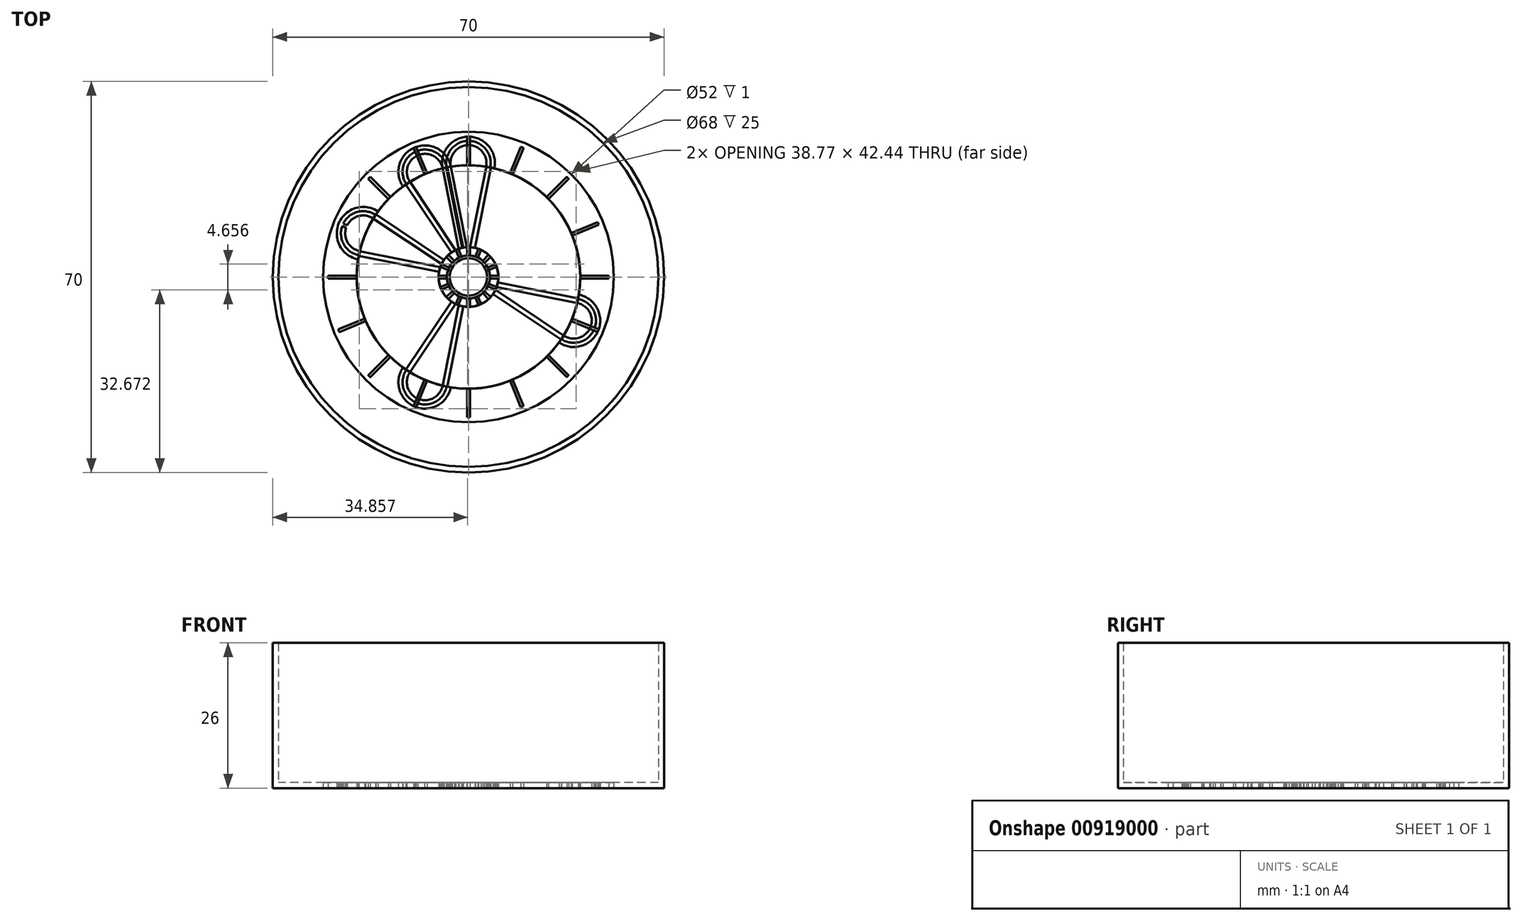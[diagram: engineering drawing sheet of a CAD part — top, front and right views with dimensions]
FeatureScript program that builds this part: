
annotation { "Feature Type Name" : "Feature", "Feature Type Description" : "" }
export const myFeature = defineFeature(function(context is Context, id is Id, definition is map)
    precondition{}
    {
        {
            var Q0;
            Q0=qCreatedBy(makeId("Top.planeOp"),FACE);
            var sketch = newSketch(context, id + "F0", { "sketchPlane" : qUnion([Q0])});
            skCircle(sketch, "E0", {"center": v(0, 0) * mm, "radius": 20 * mm});
            skLineSegment(sketch, "E1", {"start": v(0, 3.84) * mm, "end": v(0, 25.12) * mm});
            skLineSegment(sketch, "E2", {"start": v(-1.04, 5.24) * mm, "end": v(-3.9, 19.62) * mm});
            skLineSegment(sketch, "E3.trimOffspring", {"start": v(-0.3, 5.34) * mm, "end": v(-3.16, 19.75) * mm});
            skCircle(sketch, "E4", {"center": v(0, 0) * mm, "radius": 3.84 * mm});
            skCircle(sketch, "E5.0", {"center": v(0, 0) * mm, "radius": 5.34 * mm});
            skLineSegment(sketch, "E6.trimOffspring", {"start": v(1.04, 5.24) * mm, "end": v(3.9, 19.62) * mm});
            skArc(sketch, "E7", {"start": v(-3.9, 19.62) * mm, "mid": v(0, 24.37) * mm, "end": v(3.9, 19.62) * mm});
            skLineSegment(sketch, "E8.0", {"start": v(0.3, 5.34) * mm, "end": v(3.16, 19.75) * mm});
            skArc(sketch, "E9.0", {"start": v(-4.63, 19.46) * mm, "mid": v(0, 25.12) * mm, "end": v(4.63, 19.46) * mm});
            skArc(sketch, "E10", {"start": v(-3.16, 19.75) * mm, "mid": v(0, 23.6) * mm, "end": v(3.16, 19.75) * mm});
            skLineSegment(sketch, "E11.0", {"start": v(-1.14, 5.22) * mm, "end": v(-4, 19.6) * mm});
            skLineSegment(sketch, "E12.0", {"start": v(1.14, 5.22) * mm, "end": v(4, 19.6) * mm});
            skCircle(sketch, "E13", {"center": v(0, 0) * mm, "radius": 26 * mm});
            skPoint(sketch, "E14.orphan", {"position": v(0, 20) * mm});
            skLineSegment(sketch, "E15.0", {"start": v(0.25, 3.84) * mm, "end": v(0.25, 25.11) * mm});
            skLineSegment(sketch, "E16.0", {"start": v(-0.25, 3.84) * mm, "end": v(-0.25, 25.11) * mm});
            skSolve(sketch);
        }
        {
            var Q0;
            {var subQ0=sQuery(id+"F0.wireOp",EDGE,"E6.trimOffspring");Q0=makeQuery(id+"F0.imprint","IMPRINT",FACE,{"disambiguationData":[TD([[makeQuery(id+"F0.imprint","IMPRINT",EDGE,{"derivedFrom":subQ0}),1.0]])]});}
            var Q1;
            {var subQ0=sQuery(id+"F0.wireOp",EDGE,"E4");var subQ1=sQuery(id+"F0.wireOp",EDGE,"E1");var subQ2=makeQuery(id+"F0.imprint","INTERSECT",VERTEX,{"derivedFrom":[subQ1,subQ0]});Q1=makeQuery(id+"F0.imprint","IMPRINT",FACE,{"disambiguationData":[TD([[makeQuery(id+"F0.imprint","IMPRINT",EDGE,{"disambiguationData":[TD([[subQ2,-1.0]])],"derivedFrom":subQ1}),-1.0]])]});}
            var Q2;
            {var subQ0=sQuery(id+"F0.wireOp",EDGE,"E4");var subQ1=sQuery(id+"F0.wireOp",EDGE,"E1");var subQ2=makeQuery(id+"F0.imprint","INTERSECT",VERTEX,{"derivedFrom":[subQ1,subQ0]});Q2=makeQuery(id+"F0.imprint","IMPRINT",FACE,{"disambiguationData":[TD([[makeQuery(id+"F0.imprint","IMPRINT",EDGE,{"disambiguationData":[TD([[subQ2,-1.0]])],"derivedFrom":subQ1}),1.0]])]});}
            var Q3;
            {var subQ0=sQuery(id+"F0.wireOp",EDGE,"E2");Q3=makeQuery(id+"F0.imprint","IMPRINT",FACE,{"disambiguationData":[TD([[makeQuery(id+"F0.imprint","IMPRINT",EDGE,{"derivedFrom":subQ0}),-1.0]])]});}
            var Q4;
            {var subQ0=sQuery(id+"F0.wireOp",EDGE,"E7");var subQ5=sQuery(id+"F0.wireOp",EDGE,"E15.0");var subQ6=makeQuery(id+"F0.imprint","INTERSECT",VERTEX,{"derivedFrom":[subQ0,subQ5]});Q4=makeQuery(id+"F0.imprint","IMPRINT",FACE,{"disambiguationData":[TD([[makeQuery(id+"F0.imprint","IMPRINT",EDGE,{"disambiguationData":[TD([[subQ6,1.0]])],"derivedFrom":subQ5}),-1.0]])]});}
            var Q5;
            {var subQ0=sQuery(id+"F0.wireOp",EDGE,"E7");var subQ5=sQuery(id+"F0.wireOp",EDGE,"E16.0");var subQ6=makeQuery(id+"F0.imprint","INTERSECT",VERTEX,{"derivedFrom":[subQ0,subQ5]});Q5=makeQuery(id+"F0.imprint","IMPRINT",FACE,{"disambiguationData":[TD([[makeQuery(id+"F0.imprint","IMPRINT",EDGE,{"disambiguationData":[TD([[subQ6,1.0]])],"derivedFrom":subQ5}),1.0]])]});}
            var Q6;
            {var subQ0=sQuery(id+"F0.wireOp",EDGE,"E10");var subQ1=sQuery(id+"F0.wireOp",EDGE,"E1");var subQ2=makeQuery(id+"F0.imprint","INTERSECT",VERTEX,{"derivedFrom":[subQ1,subQ0]});Q6=makeQuery(id+"F0.imprint","IMPRINT",FACE,{"disambiguationData":[TD([[makeQuery(id+"F0.imprint","IMPRINT",EDGE,{"disambiguationData":[TD([[subQ2,-1.0]])],"derivedFrom":subQ1}),1.0]])]});}
            var Q7;
            {var subQ0=sQuery(id+"F0.wireOp",EDGE,"E10");var subQ1=sQuery(id+"F0.wireOp",EDGE,"E1");var subQ2=makeQuery(id+"F0.imprint","INTERSECT",VERTEX,{"derivedFrom":[subQ1,subQ0]});Q7=makeQuery(id+"F0.imprint","IMPRINT",FACE,{"disambiguationData":[TD([[makeQuery(id+"F0.imprint","IMPRINT",EDGE,{"disambiguationData":[TD([[subQ2,-1.0]])],"derivedFrom":subQ1}),-1.0]])]});}
            var Q8;
            {var subQ0=sQuery(id+"F0.wireOp",EDGE,"E2");Q8=makeQuery(id+"F0.imprint","IMPRINT",FACE,{"disambiguationData":[TD([[makeQuery(id+"F0.imprint","IMPRINT",EDGE,{"derivedFrom":subQ0}),1.0]])]});}
            var Q9;
            {var subQ0=sQuery(id+"F0.wireOp",EDGE,"E6.trimOffspring");Q9=makeQuery(id+"F0.imprint","IMPRINT",FACE,{"disambiguationData":[TD([[makeQuery(id+"F0.imprint","IMPRINT",EDGE,{"derivedFrom":subQ0}),-1.0]])]});}
            var Q10;
            {var subQ0=sQuery(id+"F0.wireOp",EDGE,"E9.0");var subQ1=sQuery(id+"F0.wireOp",EDGE,"E1");var subQ2=makeQuery(id+"F0.imprint","INTERSECT",VERTEX,{"derivedFrom":[subQ1,subQ0]});Q10=makeQuery(id+"F0.imprint","IMPRINT",FACE,{"disambiguationData":[TD([[makeQuery(id+"F0.imprint","IMPRINT",EDGE,{"disambiguationData":[TD([[subQ2,1.0]])],"derivedFrom":subQ1}),-1.0]])]});}
            var Q11;
            {var subQ0=sQuery(id+"F0.wireOp",EDGE,"E9.0");var subQ1=sQuery(id+"F0.wireOp",EDGE,"E1");var subQ2=makeQuery(id+"F0.imprint","INTERSECT",VERTEX,{"derivedFrom":[subQ1,subQ0]});Q11=makeQuery(id+"F0.imprint","IMPRINT",FACE,{"disambiguationData":[TD([[makeQuery(id+"F0.imprint","IMPRINT",EDGE,{"disambiguationData":[TD([[subQ2,1.0]])],"derivedFrom":subQ1}),1.0]])]});}
            var Q12;
            {var subQ2=sQuery(id+"F0.wireOp",EDGE,"E15.0");var subQ6=sQuery(id+"F0.wireOp",EDGE,"E4");var subQ7=makeQuery(id+"F0.imprint","INTERSECT",VERTEX,{"derivedFrom":[subQ6,subQ2]});Q12=makeQuery(id+"F0.imprint","IMPRINT",FACE,{"disambiguationData":[TD([[makeQuery(id+"F0.imprint","IMPRINT",EDGE,{"disambiguationData":[TD([[subQ7,1.0]])],"derivedFrom":subQ6}),-1.0]])]});}
            var Q13;
            {var subQ0=sQuery(id+"F0.wireOp",EDGE,"E9.0");var subQ1=sQuery(id+"F0.wireOp",EDGE,"E0");var subQ2=makeQuery(id+"F0.imprint","INTERSECT",VERTEX,{"disambiguationData":[OD(0.0)],"derivedFrom":[subQ1,subQ0]});Q13=makeQuery(id+"F0.imprint","IMPRINT",FACE,{"disambiguationData":[TD([[makeQuery(id+"F0.imprint","IMPRINT",EDGE,{"disambiguationData":[TD([[subQ2,1.0]])],"derivedFrom":subQ1}),-1.0]])]});}
            var Q14;
            {var subQ0=sQuery(id+"F0.wireOp",EDGE,"E9.0");var subQ1=sQuery(id+"F0.wireOp",EDGE,"E0");var subQ2=makeQuery(id+"F0.imprint","INTERSECT",VERTEX,{"disambiguationData":[OD(1.0)],"derivedFrom":[subQ1,subQ0]});Q14=makeQuery(id+"F0.imprint","IMPRINT",FACE,{"disambiguationData":[TD([[makeQuery(id+"F0.imprint","IMPRINT",EDGE,{"disambiguationData":[TD([[subQ2,-1.0]])],"derivedFrom":subQ1}),-1.0]])]});}
            extrude(context, id + "F1", {"entities" : qUnion([Q0, Q1, Q2, Q3, Q4, Q5, Q6, Q7, Q8, Q9, Q10, Q11, Q12, Q13, Q14]), "depth" : 1 * mm, "offsetDistance" : 25 * mm});
        }
        {
            var Q0;
            Q0=makeQuery(id+"F1.opExtrude","SWEPT_BODY",BODY,{"disambiguationData":[OSD([sQuery(id+"F0.wireOp",EDGE,"E0"),sQuery(id+"F0.wireOp",EDGE,"E2"),sQuery(id+"F0.wireOp",EDGE,"E3.trimOffspring"),sQuery(id+"F0.wireOp",EDGE,"E4"),sQuery(id+"F0.wireOp",EDGE,"E5.0"),sQuery(id+"F0.wireOp",EDGE,"E6.trimOffspring"),sQuery(id+"F0.wireOp",EDGE,"E8.0"),sQuery(id+"F0.wireOp",EDGE,"E9.0"),sQuery(id+"F0.wireOp",EDGE,"E10")])]});
            var Q1;
            Q1=makeQuery(id+"F1.opExtrude","CAP_EDGE",EDGE,{"disambiguationData":[OSD([sQuery(id+"F0.wireOp",EDGE,"E4")])],"isStart":false});
            transform(context, id + "F2", {"entities" : qUnion([Q0]), "transformType" : TransformType.ROTATION, "transformAxis" : qUnion([Q1]), "angle" : 22.5 * degree, "makeCopy" : true});
        }
        {
            var Q0;
            Q0=makeQuery(id+"F2.opPattern","COPY",BODY,{"derivedFrom":makeQuery(id+"F1.opExtrude","SWEPT_BODY",BODY,{"disambiguationData":[OSD([sQuery(id+"F0.wireOp",EDGE,"E0"),sQuery(id+"F0.wireOp",EDGE,"E3.trimOffspring"),sQuery(id+"F0.wireOp",EDGE,"E4"),sQuery(id+"F0.wireOp",EDGE,"E5.0"),sQuery(id+"F0.wireOp",EDGE,"E8.0"),sQuery(id+"F0.wireOp",EDGE,"E9.0"),sQuery(id+"F0.wireOp",EDGE,"E10"),sQuery(id+"F0.wireOp",EDGE,"E11.0"),sQuery(id+"F0.wireOp",EDGE,"E12.0")])]}),"instanceName":"1"});
            var Q1;
            Q1=sQuery(id+"F0.wireOp",EDGE,"E4");
            transform(context, id + "F3", {"entities" : qUnion([Q0]), "transformType" : TransformType.ROTATION, "transformAxis" : qUnion([Q1]), "angle" : 45 * degree, "makeCopy" : true});
        }
        {
            var Q0;
            Q0=makeQuery(id+"F3.opPattern","COPY",BODY,{"derivedFrom":makeQuery(id+"F2.opPattern","COPY",BODY,{"derivedFrom":makeQuery(id+"F1.opExtrude","SWEPT_BODY",BODY,{"disambiguationData":[OSD([sQuery(id+"F0.wireOp",EDGE,"E0"),sQuery(id+"F0.wireOp",EDGE,"E3.trimOffspring"),sQuery(id+"F0.wireOp",EDGE,"E4"),sQuery(id+"F0.wireOp",EDGE,"E5.0"),sQuery(id+"F0.wireOp",EDGE,"E8.0"),sQuery(id+"F0.wireOp",EDGE,"E9.0"),sQuery(id+"F0.wireOp",EDGE,"E10"),sQuery(id+"F0.wireOp",EDGE,"E11.0"),sQuery(id+"F0.wireOp",EDGE,"E12.0"),sQuery(id+"F0.wireOp",EDGE,"E13")])]}),"instanceName":"1"}),"instanceName":"1"});
            var Q1;
            Q1=makeQuery(id+"F3.opPattern","COPY",EDGE,{"derivedFrom":makeQuery(id+"F2.opPattern","COPY",EDGE,{"derivedFrom":makeQuery(id+"F1.opExtrude","CAP_EDGE",EDGE,{"disambiguationData":[OSD([sQuery(id+"F0.wireOp",EDGE,"E4")])],"isStart":false}),"instanceName":"1"}),"instanceName":"1"});
            transform(context, id + "F4", {"entities" : qUnion([Q0]), "transformType" : TransformType.ROTATION, "transformAxis" : qUnion([Q1]), "angle" : 90 * degree, "makeCopy" : true});
        }
        {
            var Q0;
            Q0=makeQuery(id+"F3.opPattern","COPY",BODY,{"derivedFrom":makeQuery(id+"F2.opPattern","COPY",BODY,{"derivedFrom":makeQuery(id+"F1.opExtrude","SWEPT_BODY",BODY,{"disambiguationData":[OSD([sQuery(id+"F0.wireOp",EDGE,"E0"),sQuery(id+"F0.wireOp",EDGE,"E3.trimOffspring"),sQuery(id+"F0.wireOp",EDGE,"E4"),sQuery(id+"F0.wireOp",EDGE,"E5.0"),sQuery(id+"F0.wireOp",EDGE,"E8.0"),sQuery(id+"F0.wireOp",EDGE,"E9.0"),sQuery(id+"F0.wireOp",EDGE,"E10"),sQuery(id+"F0.wireOp",EDGE,"E11.0"),sQuery(id+"F0.wireOp",EDGE,"E12.0"),sQuery(id+"F0.wireOp",EDGE,"E13")])]}),"instanceName":"1"}),"instanceName":"1"});
            var Q1;
            Q1=sQuery(id+"F0.wireOp",EDGE,"E4");
            transform(context, id + "F5", {"entities" : qUnion([Q0]), "transformType" : TransformType.ROTATION, "transformAxis" : qUnion([Q1]), "angle" : 180 * degree, "makeCopy" : true});
        }
        {
            var Q0;
            Q0=qCreatedBy(makeId("Top.planeOp"),FACE);
            var sketch = newSketch(context, id + "F6", { "sketchPlane" : qUnion([Q0])});
            skCircle(sketch, "E17", {"center": v(0, 0) * mm, "radius": 35 * mm});
            skSolve(sketch);
        }
        {
            var Q0;
            Q0=makeQuery(id+"F6.imprint","IMPRINT",FACE,{"disambiguationData":[TD([[makeQuery(id+"F6.imprint","IMPRINT",EDGE,{"derivedFrom":sQuery(id+"F6.wireOp",EDGE,"E17")}),1.0]])]});
            extrude(context, id + "F7", {"entities" : qUnion([Q0]), "depth" : 1 * mm, "offsetDistance" : 25 * mm});
        }
        {
            var Q0;
            Q0=makeQuery(id+"F3.opPattern","COPY",BODY,{"derivedFrom":makeQuery(id+"F2.opPattern","COPY",BODY,{"derivedFrom":makeQuery(id+"F1.opExtrude","SWEPT_BODY",BODY,{"disambiguationData":[OSD([sQuery(id+"F0.wireOp",EDGE,"E0"),sQuery(id+"F0.wireOp",EDGE,"E3.trimOffspring"),sQuery(id+"F0.wireOp",EDGE,"E4"),sQuery(id+"F0.wireOp",EDGE,"E5.0"),sQuery(id+"F0.wireOp",EDGE,"E8.0"),sQuery(id+"F0.wireOp",EDGE,"E9.0"),sQuery(id+"F0.wireOp",EDGE,"E10"),sQuery(id+"F0.wireOp",EDGE,"E11.0"),sQuery(id+"F0.wireOp",EDGE,"E12.0")])]}),"instanceName":"1"}),"instanceName":"1"});
            var Q1;
            Q1=makeQuery(id+"F7.opExtrude","SWEPT_BODY",BODY,{"disambiguationData":[OSD([sQuery(id+"F6.wireOp",EDGE,"E17")])]});
            booleanBodies(context, id + "F8", {"operationType" : BooleanOperationType.SUBTRACTION, "tools" : qUnion([Q0]), "targets" : qUnion([Q1])});
        }
        {
            var Q0;
            {var subQ0=sQuery(id+"F0.wireOp",EDGE,"E9.0");var subQ1=sQuery(id+"F0.wireOp",EDGE,"E1");var subQ2=makeQuery(id+"F0.imprint","INTERSECT",VERTEX,{"derivedFrom":[subQ1,subQ0]});Q0=makeQuery(id+"F0.imprint","IMPRINT",FACE,{"disambiguationData":[TD([[makeQuery(id+"F0.imprint","IMPRINT",EDGE,{"disambiguationData":[TD([[subQ2,1.0]])],"derivedFrom":subQ1}),-1.0]])]});}
            var Q1;
            {var subQ0=sQuery(id+"F0.wireOp",EDGE,"E9.0");var subQ1=sQuery(id+"F0.wireOp",EDGE,"E1");var subQ2=makeQuery(id+"F0.imprint","INTERSECT",VERTEX,{"derivedFrom":[subQ1,subQ0]});Q1=makeQuery(id+"F0.imprint","IMPRINT",FACE,{"disambiguationData":[TD([[makeQuery(id+"F0.imprint","IMPRINT",EDGE,{"disambiguationData":[TD([[subQ2,1.0]])],"derivedFrom":subQ1}),1.0]])]});}
            var Q2;
            {var subQ0=sQuery(id+"F0.wireOp",EDGE,"E10");var subQ1=sQuery(id+"F0.wireOp",EDGE,"E1");var subQ2=makeQuery(id+"F0.imprint","INTERSECT",VERTEX,{"derivedFrom":[subQ1,subQ0]});Q2=makeQuery(id+"F0.imprint","IMPRINT",FACE,{"disambiguationData":[TD([[makeQuery(id+"F0.imprint","IMPRINT",EDGE,{"disambiguationData":[TD([[subQ2,-1.0]])],"derivedFrom":subQ1}),1.0]])]});}
            var Q3;
            {var subQ0=sQuery(id+"F0.wireOp",EDGE,"E10");var subQ1=sQuery(id+"F0.wireOp",EDGE,"E1");var subQ2=makeQuery(id+"F0.imprint","INTERSECT",VERTEX,{"derivedFrom":[subQ1,subQ0]});Q3=makeQuery(id+"F0.imprint","IMPRINT",FACE,{"disambiguationData":[TD([[makeQuery(id+"F0.imprint","IMPRINT",EDGE,{"disambiguationData":[TD([[subQ2,-1.0]])],"derivedFrom":subQ1}),-1.0]])]});}
            var Q4;
            {var subQ0=sQuery(id+"F0.wireOp",EDGE,"E15.0");var subQ1=sQuery(id+"F0.wireOp",EDGE,"E0");var subQ2=makeQuery(id+"F0.imprint","INTERSECT",VERTEX,{"derivedFrom":[subQ1,subQ0]});Q4=makeQuery(id+"F0.imprint","IMPRINT",FACE,{"disambiguationData":[TD([[makeQuery(id+"F0.imprint","IMPRINT",EDGE,{"disambiguationData":[TD([[subQ2,-1.0]])],"derivedFrom":subQ1}),-1.0]])]});}
            var Q5;
            {var subQ0=sQuery(id+"F0.wireOp",EDGE,"E1");var subQ1=sQuery(id+"F0.wireOp",EDGE,"E0");var subQ2=makeQuery(id+"F0.imprint","INTERSECT",VERTEX,{"derivedFrom":[subQ1,subQ0]});Q5=makeQuery(id+"F0.imprint","IMPRINT",FACE,{"disambiguationData":[TD([[makeQuery(id+"F0.imprint","IMPRINT",EDGE,{"disambiguationData":[TD([[subQ2,-1.0]])],"derivedFrom":subQ1}),-1.0]])]});}
            var Q6;
            {var subQ0=sQuery(id+"F0.wireOp",EDGE,"E1");var subQ1=sQuery(id+"F0.wireOp",EDGE,"E0");var subQ2=makeQuery(id+"F0.imprint","INTERSECT",VERTEX,{"derivedFrom":[subQ1,subQ0]});Q6=makeQuery(id+"F0.imprint","IMPRINT",FACE,{"disambiguationData":[TD([[makeQuery(id+"F0.imprint","IMPRINT",EDGE,{"disambiguationData":[TD([[subQ2,-1.0]])],"derivedFrom":subQ1}),1.0]])]});}
            var Q7;
            {var subQ0=sQuery(id+"F0.wireOp",EDGE,"E15.0");var subQ1=sQuery(id+"F0.wireOp",EDGE,"E0");var subQ2=makeQuery(id+"F0.imprint","INTERSECT",VERTEX,{"derivedFrom":[subQ1,subQ0]});Q7=makeQuery(id+"F0.imprint","IMPRINT",FACE,{"disambiguationData":[TD([[makeQuery(id+"F0.imprint","IMPRINT",EDGE,{"disambiguationData":[TD([[subQ2,-1.0]])],"derivedFrom":subQ1}),1.0]])]});}
            var Q8;
            {var subQ0=sQuery(id+"F0.wireOp",EDGE,"E4");var subQ1=sQuery(id+"F0.wireOp",EDGE,"E1");var subQ2=makeQuery(id+"F0.imprint","INTERSECT",VERTEX,{"derivedFrom":[subQ1,subQ0]});Q8=makeQuery(id+"F0.imprint","IMPRINT",FACE,{"disambiguationData":[TD([[makeQuery(id+"F0.imprint","IMPRINT",EDGE,{"disambiguationData":[TD([[subQ2,-1.0]])],"derivedFrom":subQ1}),1.0]])]});}
            var Q9;
            {var subQ0=sQuery(id+"F0.wireOp",EDGE,"E4");var subQ1=sQuery(id+"F0.wireOp",EDGE,"E1");var subQ2=makeQuery(id+"F0.imprint","INTERSECT",VERTEX,{"derivedFrom":[subQ1,subQ0]});Q9=makeQuery(id+"F0.imprint","IMPRINT",FACE,{"disambiguationData":[TD([[makeQuery(id+"F0.imprint","IMPRINT",EDGE,{"disambiguationData":[TD([[subQ2,-1.0]])],"derivedFrom":subQ1}),-1.0]])]});}
            extrude(context, id + "F9", {"entities" : qUnion([Q0, Q1, Q2, Q3, Q4, Q5, Q6, Q7, Q8, Q9]), "depth" : 1 * mm, "offsetDistance" : 25 * mm});
        }
        {
            var Q0;
            Q0=makeQuery(id+"F9.opExtrude","SWEPT_BODY",BODY,{"disambiguationData":[OSD([sQuery(id+"F0.wireOp",EDGE,"E4"),sQuery(id+"F0.wireOp",EDGE,"E9.0"),sQuery(id+"F0.wireOp",EDGE,"E15.0"),sQuery(id+"F0.wireOp",EDGE,"E16.0")])]});
            var Q1;
            Q1=makeQuery(id+"F8.opBoolean","COPY",EDGE,{"derivedFrom":makeQuery(id+"F3.opPattern","COPY",EDGE,{"derivedFrom":makeQuery(id+"F2.opPattern","COPY",EDGE,{"derivedFrom":makeQuery(id+"F1.opExtrude","CAP_EDGE",EDGE,{"disambiguationData":[OSD([sQuery(id+"F0.wireOp",EDGE,"E4")])],"isStart":false}),"instanceName":"1"}),"instanceName":"1"})});
            transform(context, id + "F10", {"entities" : qUnion([Q0]), "transformType" : TransformType.ROTATION, "transformAxis" : qUnion([Q1]), "angle" : 22.5 * degree, "makeCopy" : true});
        }
        {
            var Q0;
            Q0=makeQuery(id+"F10.opPattern","COPY",BODY,{"derivedFrom":makeQuery(id+"F9.opExtrude","SWEPT_BODY",BODY,{"disambiguationData":[OSD([sQuery(id+"F0.wireOp",EDGE,"E4"),sQuery(id+"F0.wireOp",EDGE,"E9.0"),sQuery(id+"F0.wireOp",EDGE,"E15.0"),sQuery(id+"F0.wireOp",EDGE,"E16.0")])]}),"instanceName":"1"});
            var Q1;
            Q1=makeQuery(id+"F8.opBoolean","COPY",EDGE,{"derivedFrom":makeQuery(id+"F3.opPattern","COPY",EDGE,{"derivedFrom":makeQuery(id+"F2.opPattern","COPY",EDGE,{"derivedFrom":makeQuery(id+"F1.opExtrude","CAP_EDGE",EDGE,{"disambiguationData":[OSD([sQuery(id+"F0.wireOp",EDGE,"E4")])],"isStart":false}),"instanceName":"1"}),"instanceName":"1"})});
            transform(context, id + "F11", {"entities" : qUnion([Q0]), "transformType" : TransformType.ROTATION, "transformAxis" : qUnion([Q1]), "angle" : 22.5 * degree, "makeCopy" : true});
        }
        {
            var Q0;
            Q0=makeQuery(id+"F11.opPattern","COPY",BODY,{"derivedFrom":makeQuery(id+"F10.opPattern","COPY",BODY,{"derivedFrom":makeQuery(id+"F9.opExtrude","SWEPT_BODY",BODY,{"disambiguationData":[OSD([sQuery(id+"F0.wireOp",EDGE,"E4"),sQuery(id+"F0.wireOp",EDGE,"E9.0"),sQuery(id+"F0.wireOp",EDGE,"E15.0"),sQuery(id+"F0.wireOp",EDGE,"E16.0")])]}),"instanceName":"1"}),"instanceName":"1"});
            var Q1;
            Q1=makeQuery(id+"F8.opBoolean","COPY",EDGE,{"derivedFrom":makeQuery(id+"F3.opPattern","COPY",EDGE,{"derivedFrom":makeQuery(id+"F2.opPattern","COPY",EDGE,{"derivedFrom":makeQuery(id+"F1.opExtrude","CAP_EDGE",EDGE,{"disambiguationData":[OSD([sQuery(id+"F0.wireOp",EDGE,"E4")])],"isStart":false}),"instanceName":"1"}),"instanceName":"1"})});
            transform(context, id + "F12", {"entities" : qUnion([Q0]), "transformType" : TransformType.ROTATION, "transformAxis" : qUnion([Q1]), "angle" : 22.5 * degree, "makeCopy" : true});
        }
        {
            var Q0;
            Q0=makeQuery(id+"F12.opPattern","COPY",BODY,{"derivedFrom":makeQuery(id+"F11.opPattern","COPY",BODY,{"derivedFrom":makeQuery(id+"F10.opPattern","COPY",BODY,{"derivedFrom":makeQuery(id+"F9.opExtrude","SWEPT_BODY",BODY,{"disambiguationData":[OSD([sQuery(id+"F0.wireOp",EDGE,"E4"),sQuery(id+"F0.wireOp",EDGE,"E9.0"),sQuery(id+"F0.wireOp",EDGE,"E15.0"),sQuery(id+"F0.wireOp",EDGE,"E16.0")])]}),"instanceName":"1"}),"instanceName":"1"}),"instanceName":"1"});
            var Q1;
            Q1=makeQuery(id+"F8.opBoolean","COPY",EDGE,{"derivedFrom":makeQuery(id+"F3.opPattern","COPY",EDGE,{"derivedFrom":makeQuery(id+"F2.opPattern","COPY",EDGE,{"derivedFrom":makeQuery(id+"F1.opExtrude","CAP_EDGE",EDGE,{"disambiguationData":[OSD([sQuery(id+"F0.wireOp",EDGE,"E4")])],"isStart":false}),"instanceName":"1"}),"instanceName":"1"})});
            transform(context, id + "F13", {"entities" : qUnion([Q0]), "transformType" : TransformType.ROTATION, "transformAxis" : qUnion([Q1]), "angle" : 22.5 * degree, "makeCopy" : true});
        }
        {
            var Q0;
            Q0=makeQuery(id+"F13.opPattern","COPY",BODY,{"derivedFrom":makeQuery(id+"F12.opPattern","COPY",BODY,{"derivedFrom":makeQuery(id+"F11.opPattern","COPY",BODY,{"derivedFrom":makeQuery(id+"F10.opPattern","COPY",BODY,{"derivedFrom":makeQuery(id+"F9.opExtrude","SWEPT_BODY",BODY,{"disambiguationData":[OSD([sQuery(id+"F0.wireOp",EDGE,"E4"),sQuery(id+"F0.wireOp",EDGE,"E9.0"),sQuery(id+"F0.wireOp",EDGE,"E15.0"),sQuery(id+"F0.wireOp",EDGE,"E16.0")])]}),"instanceName":"1"}),"instanceName":"1"}),"instanceName":"1"}),"instanceName":"1"});
            var Q1;
            Q1=makeQuery(id+"F12.opPattern","COPY",BODY,{"derivedFrom":makeQuery(id+"F11.opPattern","COPY",BODY,{"derivedFrom":makeQuery(id+"F10.opPattern","COPY",BODY,{"derivedFrom":makeQuery(id+"F9.opExtrude","SWEPT_BODY",BODY,{"disambiguationData":[OSD([sQuery(id+"F0.wireOp",EDGE,"E4"),sQuery(id+"F0.wireOp",EDGE,"E9.0"),sQuery(id+"F0.wireOp",EDGE,"E15.0"),sQuery(id+"F0.wireOp",EDGE,"E16.0")])]}),"instanceName":"1"}),"instanceName":"1"}),"instanceName":"1"});
            var Q2;
            Q2=makeQuery(id+"F11.opPattern","COPY",BODY,{"derivedFrom":makeQuery(id+"F10.opPattern","COPY",BODY,{"derivedFrom":makeQuery(id+"F9.opExtrude","SWEPT_BODY",BODY,{"disambiguationData":[OSD([sQuery(id+"F0.wireOp",EDGE,"E4"),sQuery(id+"F0.wireOp",EDGE,"E9.0"),sQuery(id+"F0.wireOp",EDGE,"E15.0"),sQuery(id+"F0.wireOp",EDGE,"E16.0")])]}),"instanceName":"1"}),"instanceName":"1"});
            var Q3;
            Q3=makeQuery(id+"F10.opPattern","COPY",BODY,{"derivedFrom":makeQuery(id+"F9.opExtrude","SWEPT_BODY",BODY,{"disambiguationData":[OSD([sQuery(id+"F0.wireOp",EDGE,"E4"),sQuery(id+"F0.wireOp",EDGE,"E9.0"),sQuery(id+"F0.wireOp",EDGE,"E15.0"),sQuery(id+"F0.wireOp",EDGE,"E16.0")])]}),"instanceName":"1"});
            var Q4;
            Q4=makeQuery(id+"F9.opExtrude","SWEPT_BODY",BODY,{"disambiguationData":[OSD([sQuery(id+"F0.wireOp",EDGE,"E4"),sQuery(id+"F0.wireOp",EDGE,"E9.0"),sQuery(id+"F0.wireOp",EDGE,"E15.0"),sQuery(id+"F0.wireOp",EDGE,"E16.0")])]});
            var Q5;
            Q5=qCreatedBy(makeId("Right.planeOp"),FACE);
            mirror(context, id + "F14", {"entities" : qUnion([Q0, Q1, Q2, Q3, Q4]), "mirrorPlane" : qUnion([Q5])});
        }
        {
            var Q0;
            Q0=makeQuery(id+"F14.opPattern","COPY",BODY,{"derivedFrom":makeQuery(id+"F13.opPattern","COPY",BODY,{"derivedFrom":makeQuery(id+"F12.opPattern","COPY",BODY,{"derivedFrom":makeQuery(id+"F11.opPattern","COPY",BODY,{"derivedFrom":makeQuery(id+"F10.opPattern","COPY",BODY,{"derivedFrom":makeQuery(id+"F9.opExtrude","SWEPT_BODY",BODY,{"disambiguationData":[OSD([sQuery(id+"F0.wireOp",EDGE,"E4"),sQuery(id+"F0.wireOp",EDGE,"E9.0"),sQuery(id+"F0.wireOp",EDGE,"E15.0"),sQuery(id+"F0.wireOp",EDGE,"E16.0")])]}),"instanceName":"1"}),"instanceName":"1"}),"instanceName":"1"}),"instanceName":"1"}),"instanceName":"1"});
            var Q1;
            Q1=makeQuery(id+"F14.opPattern","COPY",BODY,{"derivedFrom":makeQuery(id+"F12.opPattern","COPY",BODY,{"derivedFrom":makeQuery(id+"F11.opPattern","COPY",BODY,{"derivedFrom":makeQuery(id+"F10.opPattern","COPY",BODY,{"derivedFrom":makeQuery(id+"F9.opExtrude","SWEPT_BODY",BODY,{"disambiguationData":[OSD([sQuery(id+"F0.wireOp",EDGE,"E4"),sQuery(id+"F0.wireOp",EDGE,"E9.0"),sQuery(id+"F0.wireOp",EDGE,"E15.0"),sQuery(id+"F0.wireOp",EDGE,"E16.0")])]}),"instanceName":"1"}),"instanceName":"1"}),"instanceName":"1"}),"instanceName":"1"});
            var Q2;
            Q2=makeQuery(id+"F14.opPattern","COPY",BODY,{"derivedFrom":makeQuery(id+"F11.opPattern","COPY",BODY,{"derivedFrom":makeQuery(id+"F10.opPattern","COPY",BODY,{"derivedFrom":makeQuery(id+"F9.opExtrude","SWEPT_BODY",BODY,{"disambiguationData":[OSD([sQuery(id+"F0.wireOp",EDGE,"E4"),sQuery(id+"F0.wireOp",EDGE,"E9.0"),sQuery(id+"F0.wireOp",EDGE,"E15.0"),sQuery(id+"F0.wireOp",EDGE,"E16.0")])]}),"instanceName":"1"}),"instanceName":"1"}),"instanceName":"1"});
            var Q3;
            Q3=makeQuery(id+"F14.opPattern","COPY",BODY,{"derivedFrom":makeQuery(id+"F10.opPattern","COPY",BODY,{"derivedFrom":makeQuery(id+"F9.opExtrude","SWEPT_BODY",BODY,{"disambiguationData":[OSD([sQuery(id+"F0.wireOp",EDGE,"E4"),sQuery(id+"F0.wireOp",EDGE,"E9.0"),sQuery(id+"F0.wireOp",EDGE,"E15.0"),sQuery(id+"F0.wireOp",EDGE,"E16.0")])]}),"instanceName":"1"}),"instanceName":"1"});
            var Q4;
            Q4=makeQuery(id+"F14.opPattern","COPY",BODY,{"derivedFrom":makeQuery(id+"F9.opExtrude","SWEPT_BODY",BODY,{"disambiguationData":[OSD([sQuery(id+"F0.wireOp",EDGE,"E4"),sQuery(id+"F0.wireOp",EDGE,"E9.0"),sQuery(id+"F0.wireOp",EDGE,"E15.0"),sQuery(id+"F0.wireOp",EDGE,"E16.0")])]}),"instanceName":"1"});
            var Q5;
            Q5=makeQuery(id+"F13.opPattern","COPY",BODY,{"derivedFrom":makeQuery(id+"F12.opPattern","COPY",BODY,{"derivedFrom":makeQuery(id+"F11.opPattern","COPY",BODY,{"derivedFrom":makeQuery(id+"F10.opPattern","COPY",BODY,{"derivedFrom":makeQuery(id+"F9.opExtrude","SWEPT_BODY",BODY,{"disambiguationData":[OSD([sQuery(id+"F0.wireOp",EDGE,"E4"),sQuery(id+"F0.wireOp",EDGE,"E9.0"),sQuery(id+"F0.wireOp",EDGE,"E15.0"),sQuery(id+"F0.wireOp",EDGE,"E16.0")])]}),"instanceName":"1"}),"instanceName":"1"}),"instanceName":"1"}),"instanceName":"1"});
            var Q6;
            Q6=makeQuery(id+"F12.opPattern","COPY",BODY,{"derivedFrom":makeQuery(id+"F11.opPattern","COPY",BODY,{"derivedFrom":makeQuery(id+"F10.opPattern","COPY",BODY,{"derivedFrom":makeQuery(id+"F9.opExtrude","SWEPT_BODY",BODY,{"disambiguationData":[OSD([sQuery(id+"F0.wireOp",EDGE,"E4"),sQuery(id+"F0.wireOp",EDGE,"E9.0"),sQuery(id+"F0.wireOp",EDGE,"E15.0"),sQuery(id+"F0.wireOp",EDGE,"E16.0")])]}),"instanceName":"1"}),"instanceName":"1"}),"instanceName":"1"});
            var Q7;
            Q7=makeQuery(id+"F11.opPattern","COPY",BODY,{"derivedFrom":makeQuery(id+"F10.opPattern","COPY",BODY,{"derivedFrom":makeQuery(id+"F9.opExtrude","SWEPT_BODY",BODY,{"disambiguationData":[OSD([sQuery(id+"F0.wireOp",EDGE,"E4"),sQuery(id+"F0.wireOp",EDGE,"E9.0"),sQuery(id+"F0.wireOp",EDGE,"E15.0"),sQuery(id+"F0.wireOp",EDGE,"E16.0")])]}),"instanceName":"1"}),"instanceName":"1"});
            var Q8;
            Q8=makeQuery(id+"F10.opPattern","COPY",BODY,{"derivedFrom":makeQuery(id+"F9.opExtrude","SWEPT_BODY",BODY,{"disambiguationData":[OSD([sQuery(id+"F0.wireOp",EDGE,"E4"),sQuery(id+"F0.wireOp",EDGE,"E9.0"),sQuery(id+"F0.wireOp",EDGE,"E15.0"),sQuery(id+"F0.wireOp",EDGE,"E16.0")])]}),"instanceName":"1"});
            var Q9;
            Q9=makeQuery(id+"F9.opExtrude","SWEPT_BODY",BODY,{"disambiguationData":[OSD([sQuery(id+"F0.wireOp",EDGE,"E4"),sQuery(id+"F0.wireOp",EDGE,"E9.0"),sQuery(id+"F0.wireOp",EDGE,"E15.0"),sQuery(id+"F0.wireOp",EDGE,"E16.0")])]});
            var Q10;
            Q10=qCreatedBy(makeId("Front.planeOp"),FACE);
            mirror(context, id + "F15", {"entities" : qUnion([Q0, Q1, Q2, Q3, Q4, Q5, Q6, Q7, Q8, Q9]), "mirrorPlane" : qUnion([Q10])});
        }
        {
            var Q0;
            Q0=makeQuery(id+"F8.opBoolean","SPLIT",BODY,{"disambiguationData":[OD(11.0)],"derivedFrom":makeQuery(id+"F7.opExtrude","SWEPT_BODY",BODY,{"disambiguationData":[OSD([sQuery(id+"F6.wireOp",EDGE,"E17")])]})});
            var Q1;
            Q1=makeQuery(id+"F8.opBoolean","SPLIT",BODY,{"disambiguationData":[OD(16.0)],"derivedFrom":makeQuery(id+"F7.opExtrude","SWEPT_BODY",BODY,{"disambiguationData":[OSD([sQuery(id+"F6.wireOp",EDGE,"E17")])]})});
            var Q2;
            Q2=makeQuery(id+"F14.opPattern","COPY",BODY,{"derivedFrom":makeQuery(id+"F10.opPattern","COPY",BODY,{"derivedFrom":makeQuery(id+"F9.opExtrude","SWEPT_BODY",BODY,{"disambiguationData":[OSD([sQuery(id+"F0.wireOp",EDGE,"E4"),sQuery(id+"F0.wireOp",EDGE,"E9.0"),sQuery(id+"F0.wireOp",EDGE,"E15.0"),sQuery(id+"F0.wireOp",EDGE,"E16.0")])]}),"instanceName":"1"}),"instanceName":"1"});
            var Q3;
            Q3=makeQuery(id+"F8.opBoolean","SPLIT",BODY,{"disambiguationData":[OD(6.0)],"derivedFrom":makeQuery(id+"F7.opExtrude","SWEPT_BODY",BODY,{"disambiguationData":[OSD([sQuery(id+"F6.wireOp",EDGE,"E17")])]})});
            var Q4;
            Q4=makeQuery(id+"F8.opBoolean","SPLIT",BODY,{"disambiguationData":[OD(14.0)],"derivedFrom":makeQuery(id+"F7.opExtrude","SWEPT_BODY",BODY,{"disambiguationData":[OSD([sQuery(id+"F6.wireOp",EDGE,"E17")])]})});
            var Q5;
            Q5=makeQuery(id+"F8.opBoolean","SPLIT",BODY,{"disambiguationData":[OD(15.0)],"derivedFrom":makeQuery(id+"F7.opExtrude","SWEPT_BODY",BODY,{"disambiguationData":[OSD([sQuery(id+"F6.wireOp",EDGE,"E17")])]})});
            var Q6;
            Q6=makeQuery(id+"F8.opBoolean","SPLIT",BODY,{"disambiguationData":[OD(13.0)],"derivedFrom":makeQuery(id+"F7.opExtrude","SWEPT_BODY",BODY,{"disambiguationData":[OSD([sQuery(id+"F6.wireOp",EDGE,"E17")])]})});
            var Q7;
            Q7=makeQuery(id+"F8.opBoolean","SPLIT",BODY,{"disambiguationData":[OD(1.0)],"derivedFrom":makeQuery(id+"F7.opExtrude","SWEPT_BODY",BODY,{"disambiguationData":[OSD([sQuery(id+"F6.wireOp",EDGE,"E17")])]})});
            var Q8;
            Q8=makeQuery(id+"F8.opBoolean","SPLIT",BODY,{"disambiguationData":[OD(12.0)],"derivedFrom":makeQuery(id+"F7.opExtrude","SWEPT_BODY",BODY,{"disambiguationData":[OSD([sQuery(id+"F6.wireOp",EDGE,"E17")])]})});
            var Q9;
            Q9=makeQuery(id+"F8.opBoolean","SPLIT",BODY,{"disambiguationData":[OD(10.0)],"derivedFrom":makeQuery(id+"F7.opExtrude","SWEPT_BODY",BODY,{"disambiguationData":[OSD([sQuery(id+"F6.wireOp",EDGE,"E17")])]})});
            var Q10;
            Q10=makeQuery(id+"F8.opBoolean","SPLIT",BODY,{"disambiguationData":[OD(9.0)],"derivedFrom":makeQuery(id+"F7.opExtrude","SWEPT_BODY",BODY,{"disambiguationData":[OSD([sQuery(id+"F6.wireOp",EDGE,"E17")])]})});
            var Q11;
            Q11=makeQuery(id+"F8.opBoolean","SPLIT",BODY,{"disambiguationData":[OD(8.0)],"derivedFrom":makeQuery(id+"F7.opExtrude","SWEPT_BODY",BODY,{"disambiguationData":[OSD([sQuery(id+"F6.wireOp",EDGE,"E17")])]})});
            var Q12;
            Q12=makeQuery(id+"F8.opBoolean","SPLIT",BODY,{"disambiguationData":[OD(7.0)],"derivedFrom":makeQuery(id+"F7.opExtrude","SWEPT_BODY",BODY,{"disambiguationData":[OSD([sQuery(id+"F6.wireOp",EDGE,"E17")])]})});
            var Q13;
            Q13=makeQuery(id+"F8.opBoolean","SPLIT",BODY,{"disambiguationData":[OD(2.0)],"derivedFrom":makeQuery(id+"F7.opExtrude","SWEPT_BODY",BODY,{"disambiguationData":[OSD([sQuery(id+"F6.wireOp",EDGE,"E17")])]})});
            var Q14;
            Q14=makeQuery(id+"F8.opBoolean","SPLIT",BODY,{"disambiguationData":[OD(3.0)],"derivedFrom":makeQuery(id+"F7.opExtrude","SWEPT_BODY",BODY,{"disambiguationData":[OSD([sQuery(id+"F6.wireOp",EDGE,"E17")])]})});
            var Q15;
            Q15=makeQuery(id+"F8.opBoolean","SPLIT",BODY,{"disambiguationData":[OD(4.0)],"derivedFrom":makeQuery(id+"F7.opExtrude","SWEPT_BODY",BODY,{"disambiguationData":[OSD([sQuery(id+"F6.wireOp",EDGE,"E17")])]})});
            var Q16;
            Q16=makeQuery(id+"F8.opBoolean","SPLIT",BODY,{"disambiguationData":[OD(5.0)],"derivedFrom":makeQuery(id+"F7.opExtrude","SWEPT_BODY",BODY,{"disambiguationData":[OSD([sQuery(id+"F6.wireOp",EDGE,"E17")])]})});
            var Q17;
            Q17=makeQuery(id+"F8.opBoolean","SPLIT",BODY,{"disambiguationData":[OD(0.0)],"derivedFrom":makeQuery(id+"F7.opExtrude","SWEPT_BODY",BODY,{"disambiguationData":[OSD([sQuery(id+"F6.wireOp",EDGE,"E17")])]})});
            var Q18;
            Q18=makeQuery(id+"F8.opBoolean","SPLIT",BODY,{"disambiguationData":[OD(17.0)],"derivedFrom":makeQuery(id+"F7.opExtrude","SWEPT_BODY",BODY,{"disambiguationData":[OSD([sQuery(id+"F6.wireOp",EDGE,"E17")])]})});
            var Q19;
            Q19=makeQuery(id+"F14.opPattern","COPY",BODY,{"derivedFrom":makeQuery(id+"F11.opPattern","COPY",BODY,{"derivedFrom":makeQuery(id+"F10.opPattern","COPY",BODY,{"derivedFrom":makeQuery(id+"F9.opExtrude","SWEPT_BODY",BODY,{"disambiguationData":[OSD([sQuery(id+"F0.wireOp",EDGE,"E4"),sQuery(id+"F0.wireOp",EDGE,"E9.0"),sQuery(id+"F0.wireOp",EDGE,"E15.0"),sQuery(id+"F0.wireOp",EDGE,"E16.0")])]}),"instanceName":"1"}),"instanceName":"1"}),"instanceName":"1"});
            var Q20;
            Q20=makeQuery(id+"F9.opExtrude","SWEPT_BODY",BODY,{"disambiguationData":[OSD([sQuery(id+"F0.wireOp",EDGE,"E4"),sQuery(id+"F0.wireOp",EDGE,"E9.0"),sQuery(id+"F0.wireOp",EDGE,"E15.0"),sQuery(id+"F0.wireOp",EDGE,"E16.0")])]});
            var Q21;
            Q21=makeQuery(id+"F14.opPattern","COPY",BODY,{"derivedFrom":makeQuery(id+"F12.opPattern","COPY",BODY,{"derivedFrom":makeQuery(id+"F11.opPattern","COPY",BODY,{"derivedFrom":makeQuery(id+"F10.opPattern","COPY",BODY,{"derivedFrom":makeQuery(id+"F9.opExtrude","SWEPT_BODY",BODY,{"disambiguationData":[OSD([sQuery(id+"F0.wireOp",EDGE,"E4"),sQuery(id+"F0.wireOp",EDGE,"E9.0"),sQuery(id+"F0.wireOp",EDGE,"E15.0"),sQuery(id+"F0.wireOp",EDGE,"E16.0")])]}),"instanceName":"1"}),"instanceName":"1"}),"instanceName":"1"}),"instanceName":"1"});
            var Q22;
            Q22=makeQuery(id+"F14.opPattern","COPY",BODY,{"derivedFrom":makeQuery(id+"F13.opPattern","COPY",BODY,{"derivedFrom":makeQuery(id+"F12.opPattern","COPY",BODY,{"derivedFrom":makeQuery(id+"F11.opPattern","COPY",BODY,{"derivedFrom":makeQuery(id+"F10.opPattern","COPY",BODY,{"derivedFrom":makeQuery(id+"F9.opExtrude","SWEPT_BODY",BODY,{"disambiguationData":[OSD([sQuery(id+"F0.wireOp",EDGE,"E4"),sQuery(id+"F0.wireOp",EDGE,"E9.0"),sQuery(id+"F0.wireOp",EDGE,"E15.0"),sQuery(id+"F0.wireOp",EDGE,"E16.0")])]}),"instanceName":"1"}),"instanceName":"1"}),"instanceName":"1"}),"instanceName":"1"}),"instanceName":"1"});
            var Q23;
            Q23=makeQuery(id+"F15.opPattern","COPY",BODY,{"derivedFrom":makeQuery(id+"F9.opExtrude","SWEPT_BODY",BODY,{"disambiguationData":[OSD([sQuery(id+"F0.wireOp",EDGE,"E4"),sQuery(id+"F0.wireOp",EDGE,"E9.0"),sQuery(id+"F0.wireOp",EDGE,"E15.0"),sQuery(id+"F0.wireOp",EDGE,"E16.0")])]}),"instanceName":"1"});
            var Q24;
            Q24=makeQuery(id+"F15.opPattern","COPY",BODY,{"derivedFrom":makeQuery(id+"F10.opPattern","COPY",BODY,{"derivedFrom":makeQuery(id+"F9.opExtrude","SWEPT_BODY",BODY,{"disambiguationData":[OSD([sQuery(id+"F0.wireOp",EDGE,"E4"),sQuery(id+"F0.wireOp",EDGE,"E9.0"),sQuery(id+"F0.wireOp",EDGE,"E15.0"),sQuery(id+"F0.wireOp",EDGE,"E16.0")])]}),"instanceName":"1"}),"instanceName":"1"});
            var Q25;
            Q25=makeQuery(id+"F10.opPattern","COPY",BODY,{"derivedFrom":makeQuery(id+"F9.opExtrude","SWEPT_BODY",BODY,{"disambiguationData":[OSD([sQuery(id+"F0.wireOp",EDGE,"E4"),sQuery(id+"F0.wireOp",EDGE,"E9.0"),sQuery(id+"F0.wireOp",EDGE,"E15.0"),sQuery(id+"F0.wireOp",EDGE,"E16.0")])]}),"instanceName":"1"});
            var Q26;
            Q26=makeQuery(id+"F11.opPattern","COPY",BODY,{"derivedFrom":makeQuery(id+"F10.opPattern","COPY",BODY,{"derivedFrom":makeQuery(id+"F9.opExtrude","SWEPT_BODY",BODY,{"disambiguationData":[OSD([sQuery(id+"F0.wireOp",EDGE,"E4"),sQuery(id+"F0.wireOp",EDGE,"E9.0"),sQuery(id+"F0.wireOp",EDGE,"E15.0"),sQuery(id+"F0.wireOp",EDGE,"E16.0")])]}),"instanceName":"1"}),"instanceName":"1"});
            var Q27;
            Q27=makeQuery(id+"F12.opPattern","COPY",BODY,{"derivedFrom":makeQuery(id+"F11.opPattern","COPY",BODY,{"derivedFrom":makeQuery(id+"F10.opPattern","COPY",BODY,{"derivedFrom":makeQuery(id+"F9.opExtrude","SWEPT_BODY",BODY,{"disambiguationData":[OSD([sQuery(id+"F0.wireOp",EDGE,"E4"),sQuery(id+"F0.wireOp",EDGE,"E9.0"),sQuery(id+"F0.wireOp",EDGE,"E15.0"),sQuery(id+"F0.wireOp",EDGE,"E16.0")])]}),"instanceName":"1"}),"instanceName":"1"}),"instanceName":"1"});
            var Q28;
            Q28=makeQuery(id+"F13.opPattern","COPY",BODY,{"derivedFrom":makeQuery(id+"F12.opPattern","COPY",BODY,{"derivedFrom":makeQuery(id+"F11.opPattern","COPY",BODY,{"derivedFrom":makeQuery(id+"F10.opPattern","COPY",BODY,{"derivedFrom":makeQuery(id+"F9.opExtrude","SWEPT_BODY",BODY,{"disambiguationData":[OSD([sQuery(id+"F0.wireOp",EDGE,"E4"),sQuery(id+"F0.wireOp",EDGE,"E9.0"),sQuery(id+"F0.wireOp",EDGE,"E15.0"),sQuery(id+"F0.wireOp",EDGE,"E16.0")])]}),"instanceName":"1"}),"instanceName":"1"}),"instanceName":"1"}),"instanceName":"1"});
            var Q29;
            Q29=makeQuery(id+"F15.opPattern","COPY",BODY,{"derivedFrom":makeQuery(id+"F11.opPattern","COPY",BODY,{"derivedFrom":makeQuery(id+"F10.opPattern","COPY",BODY,{"derivedFrom":makeQuery(id+"F9.opExtrude","SWEPT_BODY",BODY,{"disambiguationData":[OSD([sQuery(id+"F0.wireOp",EDGE,"E4"),sQuery(id+"F0.wireOp",EDGE,"E9.0"),sQuery(id+"F0.wireOp",EDGE,"E15.0"),sQuery(id+"F0.wireOp",EDGE,"E16.0")])]}),"instanceName":"1"}),"instanceName":"1"}),"instanceName":"1"});
            var Q30;
            Q30=makeQuery(id+"F15.opPattern","COPY",BODY,{"derivedFrom":makeQuery(id+"F12.opPattern","COPY",BODY,{"derivedFrom":makeQuery(id+"F11.opPattern","COPY",BODY,{"derivedFrom":makeQuery(id+"F10.opPattern","COPY",BODY,{"derivedFrom":makeQuery(id+"F9.opExtrude","SWEPT_BODY",BODY,{"disambiguationData":[OSD([sQuery(id+"F0.wireOp",EDGE,"E4"),sQuery(id+"F0.wireOp",EDGE,"E9.0"),sQuery(id+"F0.wireOp",EDGE,"E15.0"),sQuery(id+"F0.wireOp",EDGE,"E16.0")])]}),"instanceName":"1"}),"instanceName":"1"}),"instanceName":"1"}),"instanceName":"1"});
            var Q31;
            Q31=makeQuery(id+"F15.opPattern","COPY",BODY,{"derivedFrom":makeQuery(id+"F14.opPattern","COPY",BODY,{"derivedFrom":makeQuery(id+"F10.opPattern","COPY",BODY,{"derivedFrom":makeQuery(id+"F9.opExtrude","SWEPT_BODY",BODY,{"disambiguationData":[OSD([sQuery(id+"F0.wireOp",EDGE,"E4"),sQuery(id+"F0.wireOp",EDGE,"E9.0"),sQuery(id+"F0.wireOp",EDGE,"E15.0"),sQuery(id+"F0.wireOp",EDGE,"E16.0")])]}),"instanceName":"1"}),"instanceName":"1"}),"instanceName":"1"});
            var Q32;
            Q32=makeQuery(id+"F15.opPattern","COPY",BODY,{"derivedFrom":makeQuery(id+"F14.opPattern","COPY",BODY,{"derivedFrom":makeQuery(id+"F11.opPattern","COPY",BODY,{"derivedFrom":makeQuery(id+"F10.opPattern","COPY",BODY,{"derivedFrom":makeQuery(id+"F9.opExtrude","SWEPT_BODY",BODY,{"disambiguationData":[OSD([sQuery(id+"F0.wireOp",EDGE,"E4"),sQuery(id+"F0.wireOp",EDGE,"E9.0"),sQuery(id+"F0.wireOp",EDGE,"E15.0"),sQuery(id+"F0.wireOp",EDGE,"E16.0")])]}),"instanceName":"1"}),"instanceName":"1"}),"instanceName":"1"}),"instanceName":"1"});
            var Q33;
            Q33=makeQuery(id+"F15.opPattern","COPY",BODY,{"derivedFrom":makeQuery(id+"F14.opPattern","COPY",BODY,{"derivedFrom":makeQuery(id+"F12.opPattern","COPY",BODY,{"derivedFrom":makeQuery(id+"F11.opPattern","COPY",BODY,{"derivedFrom":makeQuery(id+"F10.opPattern","COPY",BODY,{"derivedFrom":makeQuery(id+"F9.opExtrude","SWEPT_BODY",BODY,{"disambiguationData":[OSD([sQuery(id+"F0.wireOp",EDGE,"E4"),sQuery(id+"F0.wireOp",EDGE,"E9.0"),sQuery(id+"F0.wireOp",EDGE,"E15.0"),sQuery(id+"F0.wireOp",EDGE,"E16.0")])]}),"instanceName":"1"}),"instanceName":"1"}),"instanceName":"1"}),"instanceName":"1"}),"instanceName":"1"});
            var Q34;
            Q34=makeQuery(id+"F14.opPattern","COPY",BODY,{"derivedFrom":makeQuery(id+"F9.opExtrude","SWEPT_BODY",BODY,{"disambiguationData":[OSD([sQuery(id+"F0.wireOp",EDGE,"E4"),sQuery(id+"F0.wireOp",EDGE,"E9.0"),sQuery(id+"F0.wireOp",EDGE,"E15.0"),sQuery(id+"F0.wireOp",EDGE,"E16.0")])]}),"instanceName":"1"});
            var Q35;
            Q35=makeQuery(id+"F15.opPattern","COPY",BODY,{"derivedFrom":makeQuery(id+"F13.opPattern","COPY",BODY,{"derivedFrom":makeQuery(id+"F12.opPattern","COPY",BODY,{"derivedFrom":makeQuery(id+"F11.opPattern","COPY",BODY,{"derivedFrom":makeQuery(id+"F10.opPattern","COPY",BODY,{"derivedFrom":makeQuery(id+"F9.opExtrude","SWEPT_BODY",BODY,{"disambiguationData":[OSD([sQuery(id+"F0.wireOp",EDGE,"E4"),sQuery(id+"F0.wireOp",EDGE,"E9.0"),sQuery(id+"F0.wireOp",EDGE,"E15.0"),sQuery(id+"F0.wireOp",EDGE,"E16.0")])]}),"instanceName":"1"}),"instanceName":"1"}),"instanceName":"1"}),"instanceName":"1"}),"instanceName":"1"});
            var Q36;
            Q36=makeQuery(id+"F15.opPattern","COPY",BODY,{"derivedFrom":makeQuery(id+"F14.opPattern","COPY",BODY,{"derivedFrom":makeQuery(id+"F9.opExtrude","SWEPT_BODY",BODY,{"disambiguationData":[OSD([sQuery(id+"F0.wireOp",EDGE,"E4"),sQuery(id+"F0.wireOp",EDGE,"E9.0"),sQuery(id+"F0.wireOp",EDGE,"E15.0"),sQuery(id+"F0.wireOp",EDGE,"E16.0")])]}),"instanceName":"1"}),"instanceName":"1"});
            var Q37;
            Q37=makeQuery(id+"F15.opPattern","COPY",BODY,{"derivedFrom":makeQuery(id+"F14.opPattern","COPY",BODY,{"derivedFrom":makeQuery(id+"F13.opPattern","COPY",BODY,{"derivedFrom":makeQuery(id+"F12.opPattern","COPY",BODY,{"derivedFrom":makeQuery(id+"F11.opPattern","COPY",BODY,{"derivedFrom":makeQuery(id+"F10.opPattern","COPY",BODY,{"derivedFrom":makeQuery(id+"F9.opExtrude","SWEPT_BODY",BODY,{"disambiguationData":[OSD([sQuery(id+"F0.wireOp",EDGE,"E4"),sQuery(id+"F0.wireOp",EDGE,"E9.0"),sQuery(id+"F0.wireOp",EDGE,"E15.0"),sQuery(id+"F0.wireOp",EDGE,"E16.0")])]}),"instanceName":"1"}),"instanceName":"1"}),"instanceName":"1"}),"instanceName":"1"}),"instanceName":"1"}),"instanceName":"1"});
            booleanBodies(context, id + "F16", {"operationType" : BooleanOperationType.UNION, "tools" : qUnion([Q0, Q1, Q2, Q3, Q4, Q5, Q6, Q7, Q8, Q9, Q10, Q11, Q12, Q13, Q14, Q15, Q16, Q17, Q18, Q19, Q20, Q21, Q22, Q23, Q24, Q25, Q26, Q27, Q28, Q29, Q30, Q31, Q32, Q33, Q34, Q35, Q36, Q37])});
        }
        {
            var Q0;
            {var subQ0=sQuery(id+"F0.wireOp",EDGE,"E16.0");var subQ1=sQuery(id+"F0.wireOp",EDGE,"E15.0");var subQ2=sQuery(id+"F0.wireOp",EDGE,"E9.0");var subQ3=sQuery(id+"F0.wireOp",EDGE,"E4");var subQ4=makeQuery(id+"F9.opExtrude","CAP_FACE",FACE,{"disambiguationData":[OSD([subQ3,subQ2,subQ1,subQ0])],"isStart":false});var subQ5=makeQuery(id+"F10.opPattern","COPY",FACE,{"derivedFrom":subQ4,"instanceName":"1"});var subQ6=makeQuery(id+"F11.opPattern","COPY",FACE,{"derivedFrom":subQ5,"instanceName":"1"});var subQ7=makeQuery(id+"F12.opPattern","COPY",FACE,{"derivedFrom":subQ6,"instanceName":"1"});var subQ8=makeQuery(id+"F14.opPattern","COPY",FACE,{"derivedFrom":subQ7,"instanceName":"1"});var subQ9=makeQuery(id+"F14.opPattern","COPY",FACE,{"derivedFrom":subQ6,"instanceName":"1"});var subQ10=makeQuery(id+"F14.opPattern","COPY",FACE,{"derivedFrom":subQ5,"instanceName":"1"});var subQ11=makeQuery(id+"F13.opPattern","COPY",FACE,{"derivedFrom":subQ7,"instanceName":"1"});var subQ17=sQuery(id+"F0.wireOp",EDGE,"E3.trimOffspring");var subQ25=makeQuery(id+"F1.opExtrude","SWEPT_FACE",FACE,{"disambiguationData":[OSD([subQ17])]});var subQ26=makeQuery(id+"F2.opPattern","COPY",FACE,{"derivedFrom":subQ25,"instanceName":"1"});var subQ27=makeQuery(id+"F3.opPattern","COPY",FACE,{"derivedFrom":subQ26,"instanceName":"1"});var subQ28=makeQuery(id+"F4.opPattern","COPY",FACE,{"derivedFrom":subQ27,"instanceName":"1"});var subQ37=sQuery(id+"F6.wireOp",EDGE,"E17");var subQ38=makeQuery(id+"F7.opExtrude","CAP_FACE",FACE,{"disambiguationData":[OSD([subQ37])],"isStart":false});var subQ39=makeQuery(id+"F3.opPattern","COPY",FACE,{"derivedFrom":subQ25,"instanceName":"1"});var subQ40=makeQuery(id+"F4.opPattern","COPY",FACE,{"derivedFrom":subQ39,"instanceName":"1"});var subQ46=makeQuery(id+"F4.opPattern","COPY",FACE,{"derivedFrom":subQ26,"instanceName":"1"});var subQ48=makeQuery(id+"F4.opPattern","COPY",FACE,{"derivedFrom":subQ25,"instanceName":"1"});var subQ54=makeQuery(id+"F1.opExtrude","SWEPT_FACE",FACE,{"disambiguationData":[OSD([subQ2])]});Q0=makeQuery(id+"F16.opBoolean","MERGE",FACE,{"derivedFrom":[makeQuery(id+"F8.opBoolean","SPLIT",FACE,{"disambiguationData":[TD([subQ54])],"derivedFrom":subQ38}),makeQuery(id+"F8.opBoolean","SPLIT",FACE,{"disambiguationData":[TD([subQ25])],"derivedFrom":subQ38}),makeQuery(id+"F8.opBoolean","SPLIT",FACE,{"disambiguationData":[TD([subQ26])],"derivedFrom":subQ38}),makeQuery(id+"F8.opBoolean","SPLIT",FACE,{"disambiguationData":[TD([subQ39])],"derivedFrom":subQ38}),makeQuery(id+"F8.opBoolean","SPLIT",FACE,{"disambiguationData":[TD([subQ27])],"derivedFrom":subQ38}),makeQuery(id+"F8.opBoolean","SPLIT",FACE,{"disambiguationData":[TD([makeQuery(id+"F3.opPattern","COPY",FACE,{"derivedFrom":makeQuery(id+"F2.opPattern","COPY",FACE,{"derivedFrom":makeQuery(id+"F1.opExtrude","SWEPT_FACE",FACE,{"disambiguationData":[OSD([subQ3])]}),"instanceName":"1"}),"instanceName":"1"})])],"derivedFrom":subQ38}),makeQuery(id+"F8.opBoolean","SPLIT",FACE,{"disambiguationData":[TD([subQ48])],"derivedFrom":subQ38}),makeQuery(id+"F8.opBoolean","SPLIT",FACE,{"disambiguationData":[TD([subQ46])],"derivedFrom":subQ38}),makeQuery(id+"F8.opBoolean","SPLIT",FACE,{"disambiguationData":[TD([subQ40])],"derivedFrom":subQ38}),makeQuery(id+"F8.opBoolean","SPLIT",FACE,{"disambiguationData":[TD([subQ28])],"derivedFrom":subQ38}),makeQuery(id+"F8.opBoolean","SPLIT",FACE,{"disambiguationData":[TD([makeQuery(id+"F5.opPattern","COPY",FACE,{"derivedFrom":subQ25,"instanceName":"1"})])],"derivedFrom":subQ38}),makeQuery(id+"F8.opBoolean","SPLIT",FACE,{"disambiguationData":[TD([makeQuery(id+"F5.opPattern","COPY",FACE,{"derivedFrom":subQ26,"instanceName":"1"})])],"derivedFrom":subQ38}),makeQuery(id+"F8.opBoolean","SPLIT",FACE,{"disambiguationData":[TD([makeQuery(id+"F5.opPattern","COPY",FACE,{"derivedFrom":subQ39,"instanceName":"1"})])],"derivedFrom":subQ38}),makeQuery(id+"F8.opBoolean","SPLIT",FACE,{"disambiguationData":[TD([makeQuery(id+"F5.opPattern","COPY",FACE,{"derivedFrom":subQ27,"instanceName":"1"})])],"derivedFrom":subQ38}),makeQuery(id+"F8.opBoolean","SPLIT",FACE,{"disambiguationData":[TD([makeQuery(id+"F5.opPattern","COPY",FACE,{"derivedFrom":subQ48,"instanceName":"1"})])],"derivedFrom":subQ38}),makeQuery(id+"F8.opBoolean","SPLIT",FACE,{"disambiguationData":[TD([makeQuery(id+"F5.opPattern","COPY",FACE,{"derivedFrom":subQ46,"instanceName":"1"})])],"derivedFrom":subQ38}),makeQuery(id+"F8.opBoolean","SPLIT",FACE,{"disambiguationData":[TD([makeQuery(id+"F5.opPattern","COPY",FACE,{"derivedFrom":subQ40,"instanceName":"1"})])],"derivedFrom":subQ38}),makeQuery(id+"F8.opBoolean","SPLIT",FACE,{"disambiguationData":[TD([makeQuery(id+"F5.opPattern","COPY",FACE,{"derivedFrom":subQ28,"instanceName":"1"})])],"derivedFrom":subQ38}),subQ4,subQ5,subQ6,subQ7,subQ11,subQ10,subQ9,subQ8,makeQuery(id+"F14.opPattern","COPY",FACE,{"derivedFrom":subQ11,"instanceName":"1"}),makeQuery(id+"F15.opPattern","COPY",FACE,{"derivedFrom":subQ4,"instanceName":"1"}),makeQuery(id+"F15.opPattern","COPY",FACE,{"derivedFrom":subQ5,"instanceName":"1"}),makeQuery(id+"F15.opPattern","COPY",FACE,{"derivedFrom":subQ6,"instanceName":"1"}),makeQuery(id+"F15.opPattern","COPY",FACE,{"derivedFrom":subQ7,"instanceName":"1"}),makeQuery(id+"F15.opPattern","COPY",FACE,{"derivedFrom":subQ10,"instanceName":"1"}),makeQuery(id+"F15.opPattern","COPY",FACE,{"derivedFrom":subQ9,"instanceName":"1"}),makeQuery(id+"F15.opPattern","COPY",FACE,{"derivedFrom":subQ8,"instanceName":"1"})]});}
            var sketch = newSketch(context, id + "F17", { "sketchPlane" : qUnion([Q0])});
            skCircle(sketch, "E18", {"center": v(0, 0) * mm, "radius": 35 * mm});
            skCircle(sketch, "E19.0", {"center": v(0, 0) * mm, "radius": 34 * mm});
            skCircle(sketch, "E20", {"center": v(0, 0) * mm, "radius": 3.84 * mm});
            skCircle(sketch, "E21", {"center": v(0, 0) * mm, "radius": 3.34 * mm});
            skSolve(sketch);
        }
        {
            var Q0;
            Q0=makeQuery(id+"F17.imprint","IMPRINT",FACE,{"disambiguationData":[TD([[makeQuery(id+"F17.imprint","IMPRINT",EDGE,{"derivedFrom":sQuery(id+"F17.wireOp",EDGE,"E18")}),1.0]])]});
            extrude(context, id + "F18", {"entities" : qUnion([Q0]), "operationType" : NewBodyOperationType.ADD, "depth" : 25 * mm, "offsetDistance" : 25 * mm});
        }
        {
            var Q0;
            Q0=makeQuery(id+"F17.imprint","IMPRINT",FACE,{"disambiguationData":[TD([[makeQuery(id+"F17.imprint","IMPRINT",EDGE,{"derivedFrom":sQuery(id+"F17.wireOp",EDGE,"E21")}),1.0]])]});
            extrude(context, id + "F19", {"entities" : qUnion([Q0]), "operationType" : NewBodyOperationType.REMOVE, "oppositeDirection" : true, "depth" : 25 * mm, "offsetDistance" : 25 * mm});
        }
    });
